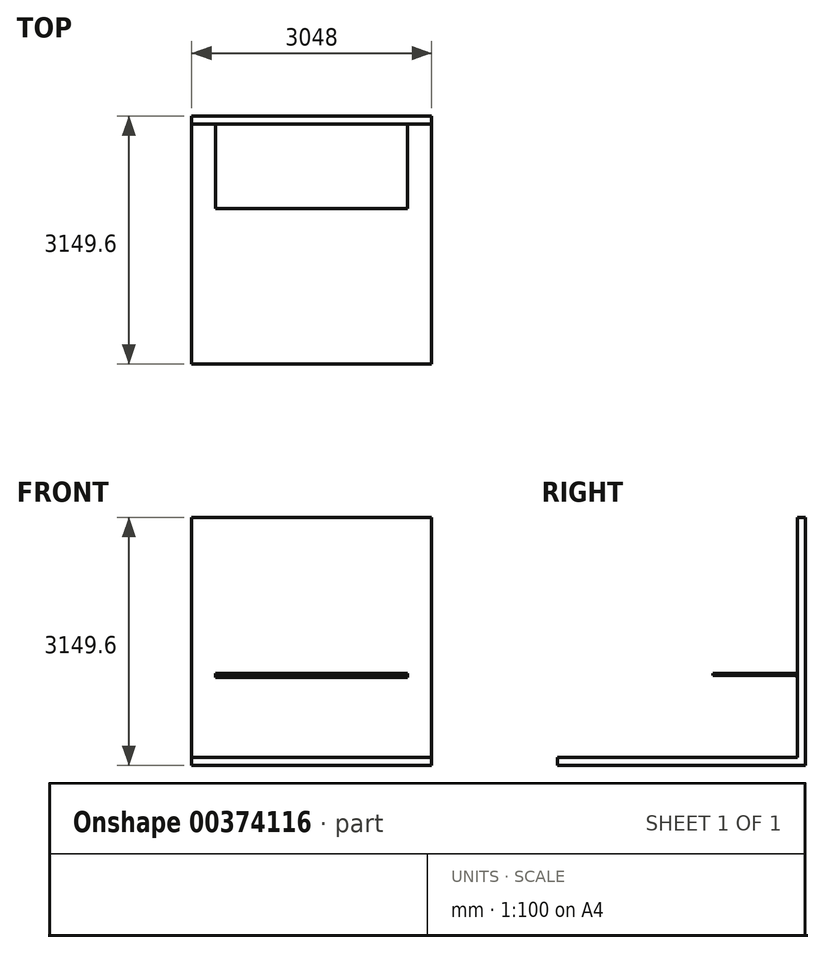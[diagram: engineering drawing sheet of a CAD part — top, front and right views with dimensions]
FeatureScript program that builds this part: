
annotation { "Feature Type Name" : "Feature", "Feature Type Description" : "" }
export const myFeature = defineFeature(function(context is Context, id is Id, definition is map)
    precondition{}
    {
        {
            var Q0;
            Q0=qCreatedBy(makeId("Right.planeOp"),FACE);
            var sketch = newSketch(context, id + "F0", { "sketchPlane" : qUnion([Q0])});
            skLineSegment(sketch, "E0.bottom", {"start": v(-3048, 0) * mm, "end": v(0, 0) * mm});
            skLineSegment(sketch, "E0.left", {"start": v(-3048, 0) * mm, "end": v(-3048, -101.6) * mm});
            skLineSegment(sketch, "E1.top", {"start": v(0, 3048) * mm, "end": v(101.6, 3048) * mm});
            skLineSegment(sketch, "E1.left", {"start": v(0, 0) * mm, "end": v(0, 3048) * mm});
            skLineSegment(sketch, "E1.right", {"start": v(101.6, -101.6) * mm, "end": v(101.6, 3048) * mm});
            skLineSegment(sketch, "E2", {"start": v(101.6, -101.6) * mm, "end": v(-3048, -101.6) * mm});
            skSolve(sketch);
        }
        {
            var Q0;
            Q0 = qSketchRegion(id + "F0", true);
            extrude(context, id + "F1", {"entities" : qUnion([Q0]), "endBound" : BoundingType.SYMMETRIC, "depth" : 3048 * mm});
        }
        {
            var Q0;
            Q0=qCreatedBy(makeId("Right.planeOp"),FACE);
            var sketch = newSketch(context, id + "F2", { "sketchPlane" : qUnion([Q0])});
            skLineSegment(sketch, "E3.bottom", {"start": v(-1073.15, 1066.8) * mm, "end": v(-6.35, 1066.8) * mm});
            skLineSegment(sketch, "E3.top", {"start": v(-1073.15, 1041.4) * mm, "end": v(-6.35, 1041.4) * mm});
            skLineSegment(sketch, "E3.left", {"start": v(-1073.15, 1066.8) * mm, "end": v(-1073.15, 1041.4) * mm});
            skLineSegment(sketch, "E3.right", {"start": v(-6.35, 1066.8) * mm, "end": v(-6.35, 1041.4) * mm});
            skLineSegment(sketch, "E4.bottom", {"start": v(-6.35, 1066.8) * mm, "end": v(0, 1066.8) * mm});
            skLineSegment(sketch, "E4.top", {"start": v(-6.35, 1016) * mm, "end": v(0, 1016) * mm});
            skLineSegment(sketch, "E4.left", {"start": v(-6.35, 1066.8) * mm, "end": v(-6.35, 1016) * mm});
            skLineSegment(sketch, "E4.right", {"start": v(0, 1066.8) * mm, "end": v(0, 1016) * mm});
            skSolve(sketch);
        }
        {
            var Q0;
            Q0 = qSketchRegion(id + "F2", true);
            extrude(context, id + "F3", {"entities" : qUnion([Q0]), "endBound" : BoundingType.SYMMETRIC, "depth" : 2438.4 * mm});
        }
        {
            var Q0;
            Q0=qCreatedBy(makeId("Right.planeOp"),FACE);
            cPlane(context, id + "F4", {"entities" : qUnion([Q0]), "cplaneType" : CPlaneType.OFFSET, "offset" : 914.4 * mm, "width" : 152.4 * mm, "height" : 152.4 * mm});
        }
    });
